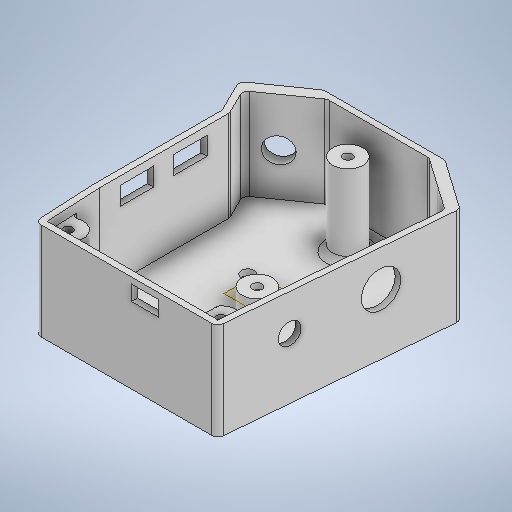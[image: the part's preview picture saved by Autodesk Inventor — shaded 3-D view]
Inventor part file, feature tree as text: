
AUTODESK INVENTOR PART (.ipt)
format: ipt  version: 2025.1 (Build 291241000, 241)  size: 481,792 bytes
history: native  units: mm
features: sketch x12, extrude x10, reference x8, other x4, fillet x3, hole x2, projected_geometry x2, shell x1, mirror x1, plane x1
ambient origin geometry x8: Origin, YZ Plane, XZ Plane, XY Plane, X Axis, Y Axis, Z Axis, Center Point
bodies: Volumenkörper1 (feature_tree)
feature tree (44):
  extrude  "Extrusion1"  Depth=20.0mm
  shell  "Wandung1"  Thickness=20.0mm
  extrude  "Extrusion6"  Depth=25.307274mm
  hole  "Bohrung1"  [1 undecoded]
  extrude  "Extrusion5"  Depth=2.0mm
  mirror  "Spiegeln1"
  extrude  "Extrusion4"  Depth=2.0mm
  extrude  "Extrusion7"  Depth=20.0mm
  extrude  "Extrusion8"  Depth=22.0mm
  plane  "Arbeitsebene1"
  extrude  "Extrusion9"  TaperAngle=0.0deg  [1 undecoded]
  hole  "Bohrung3"  [1 undecoded]
  extrude  "Extrusion10"  Depth=5.0mm
  extrude  "Extrusion11"  Depth=5.0mm
  extrude  "Extrusion12"  Depth=30.0mm TaperAngle=0.0deg
  fillet  "Rundung1"  Radius=0.5mm
  fillet  "Rundung2"  Radius=0.5mm
  fillet  "Rundung3"  Radius=30.1mm
  sketch  "Skizze1"  dims[d2=40.0mm d3=20.0mm d4=20.0mm]
  sketch  "Skizze2"  dims[d5=25.307274mm d6=25.307274mm]
  sketch  "Skizze6"  dims[d7=85.0mm d8=60.0mm]
  sketch  "Skizze7"  dims[d9=32.0mm d10=0.0mm d11=2.0mm]
  sketch  "Skizze8"  dims[d12=8.3mm d13=8.0mm d14=4.0mm d15=2.0mm d16=90.0deg d17=11.8mm d18=20.594885mm d40=12.0mm]
  projected_geometry  "Projizierte Kontur1"
  sketch  "Skizze9"  dims[d41=7.0mm d42=20.0mm]
  sketch  "Skizze10"  dims[d43=24.0mm d44=22.0mm]
  reference  "Referenz1"
  reference  "Referenz2"
  reference  "Referenz3"
  reference  "Referenz4"
  reference  "Referenz5"
  reference  "Referenz6"
  sketch  "Skizze11"  dims[d45=7.0mm d46=0.0mm]
  reference  "Referenz7"
  sketch  "Skizze13"  dims[d47=42.6mm d48=20.0mm]
  reference  "Referenz9"
  sketch  "Skizze14"  dims[d49=31.0mm d50=5.0mm]
  sketch  "Skizze15"  dims[d51=10.0mm d52=5.0mm d53=10.0mm]
  projected_geometry  "Projizierte Kontur2"
  sketch  "Skizze16"  dims[d54=7.5mm d57=30.0mm d58=0.0mm d59=0.5mm d60=0.5mm d61=30.1mm d62=5.7mm d63=3.5mm d64=3.5mm d65=32.0mm d66=0.0mm d67=10.0mm d68=3.2mm d69=9.0mm d70=0.0mm d71=0.5mm d72=9.0mm d73=0.0mm d74=10.0mm d75=3.2mm d76=-2.0mm d77=5.3mm d78=5.3mm d79=0.0mm d80=0.0mm d88=4.2mm d89=6.0mm d90=4.0mm d91=2.0mm d92=90.0deg d93=8.0mm d94=20.594885mm d95=10.0mm d96=10.0mm d97=3.0mm d98=27.0mm d99=0.0mm d100=3.0mm d101=10.0mm d102=6.0mm d103=25.2mm d104=3.0mm d105=10.0mm d106=25.2mm d107=27.0mm d108=0.0mm d109=4.0mm d110=10.0mm d111=6.0mm d112=27.0mm d113=0.0mm d114=1.5mm d115=2.0mm d116=2.0mm]
  other  "<userpath>\OneDrive\Documents\Projekte\Macrolampe\CAD\Baugruppen\Macrolight.iam"
  other  "Macrolight.iam"
  other  "Platine:1"
  other  "hotshouh mount:2"
note: 3 required parameter values undecoded (feature->parameter linkage not recoverable at this tier; creation-order binding heuristic only, values carry confidence <= 0.55)
